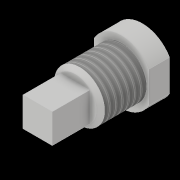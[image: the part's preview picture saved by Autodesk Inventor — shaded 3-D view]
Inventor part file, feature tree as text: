
AUTODESK INVENTOR PART (.ipt)
format: ipt  version: 2019 (Build 230136000, 136)  size: 114,688 bytes
history: native  units: mm
features: extrude x4, sketch x4, chamfer x1, thread x1
ambient origin geometry x8: Origin, YZ Plane, XZ Plane, XY Plane, X Axis, Y Axis, Z Axis, Center Point
bodies: Solid1 (feature_tree)
feature tree (10):
  extrude  "Extrusion1"  Depth=10.0mm TaperAngle=0.0deg
  extrude  "Extrusion2"  Depth=40.0mm
  extrude  "Extrusion3"  Depth=22.0mm
  chamfer  "Chamfer1"  Distance=22.0mm
  extrude  "Extrusion4"  Depth=14.0mm
  thread  "Thread1"  [1 undecoded]
  sketch  "Sketch1"  dims[d0=30.0mm d1=10.0mm d2=0.0mm]
  sketch  "Sketch2"  dims[d3=26.0mm d4=40.0mm]
  sketch  "Sketch3"  dims[d5=10.0mm d6=0.0mm d7=24.0mm d8=22.0mm d9=0.0mm]
  sketch  "Sketch4"  dims[d10=2.0mm d11=2.0mm d12=45.0deg d13=14.0mm d14=18.0mm d15=0.0mm d16=10.0mm d17=0.0mm]
note: 1 required parameter value undecoded (feature->parameter linkage not recoverable at this tier; creation-order binding heuristic only, values carry confidence <= 0.55)
